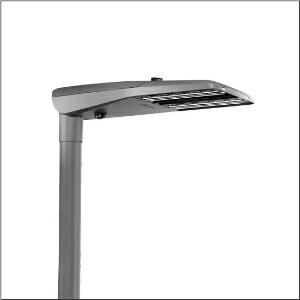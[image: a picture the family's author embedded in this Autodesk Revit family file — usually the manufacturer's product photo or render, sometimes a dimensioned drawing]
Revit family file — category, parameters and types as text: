
# Revit family: streetlight_sl_11_iq_midi___st0_5a_5xc3b51y08le_54cc
name_source: partatom
category: Lighting Fixtures
units: mm (PartAtom-declared; Revit-internal decimal feet)

## family parameters
Cut with Voids When Loaded = No
Host = Face
Light Source = No
Part Type = Normal
Room Calculation Point = No
Round Connector Dimension = Use Diameter
Shared = No

## types (1)
- --- (1 x LED, 9120 lm, 59.4 W, 3000K)
    Apparent Load = 59 VA
    CIE Flux Codes = 43 74 97 100 100
    Color Rendering = 70
    Color Temperature = 3000K
    Default Elevation = 1800 mm
    Description = Streetlight SL 11 iQ midi, mast luminaire, primary light control with 3 zone facetted reflector, of plastic, silver coated, highly specular, primary optical cover: cover, of PMMA, transparent, light distribution: ST0.5a, light emission: direct distribution, primary light characteristic: asymmetric, installation type: post-top, side-entry, LED, High Power LED, rated luminous flux: 9.120lm, luminous efficacy: 154lm/W, light colour: 730, colour temperature: 3000K, control: presetting dimming logarithmic, Street-Remote, Auto-Match, Temp-Guard, Lumen-Switch, Night-Set, Smart-Wire, Light-Fading, Desk-Remote (wireless, voltage-free reading and setting of iQ features in the workshop via application-optimized NFC function/RFID function), optimised constant luminous flux control (CLO 2.0), with cable H07RN-F 5x 1.5mm², mains connection: 230..240V, AC, 50/60Hz, connection cable pre-assembled, cable length: 8,5m, start of lifetime: 59W, end of service life: 62W, reduction: 29W, luminaire housing, of diecast aluminium, powder-coated, Siteco® metallic grey (DB 702S), please order mast flange separately, inclination adjustable without tools: 0°, 5°, 10°, 15° (post-top) | 0°, -5°, -10°, -15° (side-entry), sealing non-destructively replaceable, multi-level sealing system, length: 780mm, width: 376mm, height: 118mm, mast flange for spigot size: 42mm (side-entry): 5XC10008XM4, 60/48mm (side-entry/post-top): 5XC10108XM2, 76/60mm (side-entry/post-top): 5XC10108XM1, equipment: standard, Smart Interface below and above, protection rating (complete): IP66, insulation class (complete): insulation class II (safety insulation), certification: CE, ENEC, VDE, UKCA, impact resistance: IK09, permissible operating ambient temperature for outdoor applications: -25..+50°C, standard-compliant lighting for roads and squares, Environmental Product Declaration (EPD) tested and certified by an independent institute, packaging unit: 1 piece

Light Distribution: ST0.5a
    Height = 118 mm
    Lamp = 1 x LED
    Lamp Light Flux = 9120 lm
    Lamp Power = 59.4 W
    Lamp count = 1
    Length = 780 mm
    Luminous efficacy = 154 lm/W
    Manufacturer = Siteco
    ModVariant = No
    Model = 5XC3B51Y08LE
    Number of Poles = 1
    OnlyDefault = Yes
    Power Factor = 1
    Product Name = Streetlight SL 11 iQ midi | ST0.5a
    Product group = mast luminaire | pylon top
    ProductGroupID = 6100
    Protection Class = Protection class II
    Protection Degree = IP 66
    RLX_Detail_Level = 1
    RLX_Emergency_Light_Flux = 0 lm
    RLX_Emergency_Type = 0
    RLX_Emergency_Type_DB = No
    RlxData = <blob elided: 74213 chars, md5=239bae2b>
    Socket = socket
    Standby Power = 0 W
    System Light Flux = 9120 lm
    System Power = 59 W
    Type Comments = factory setting: luminous flux: 100 % | dim-lin: 254 | 521 mA
    Type Image = l_1004429.jpg
    URL = http://relux.com
    VarID = @adj_082263
    Voltage = 0 V
    Weight = 0.00 kg
    Width = 376 mm

## geometry (parser evidence)
native form markers: Blend x4, Sweep x12
no freeform markers — native parametric forms only
